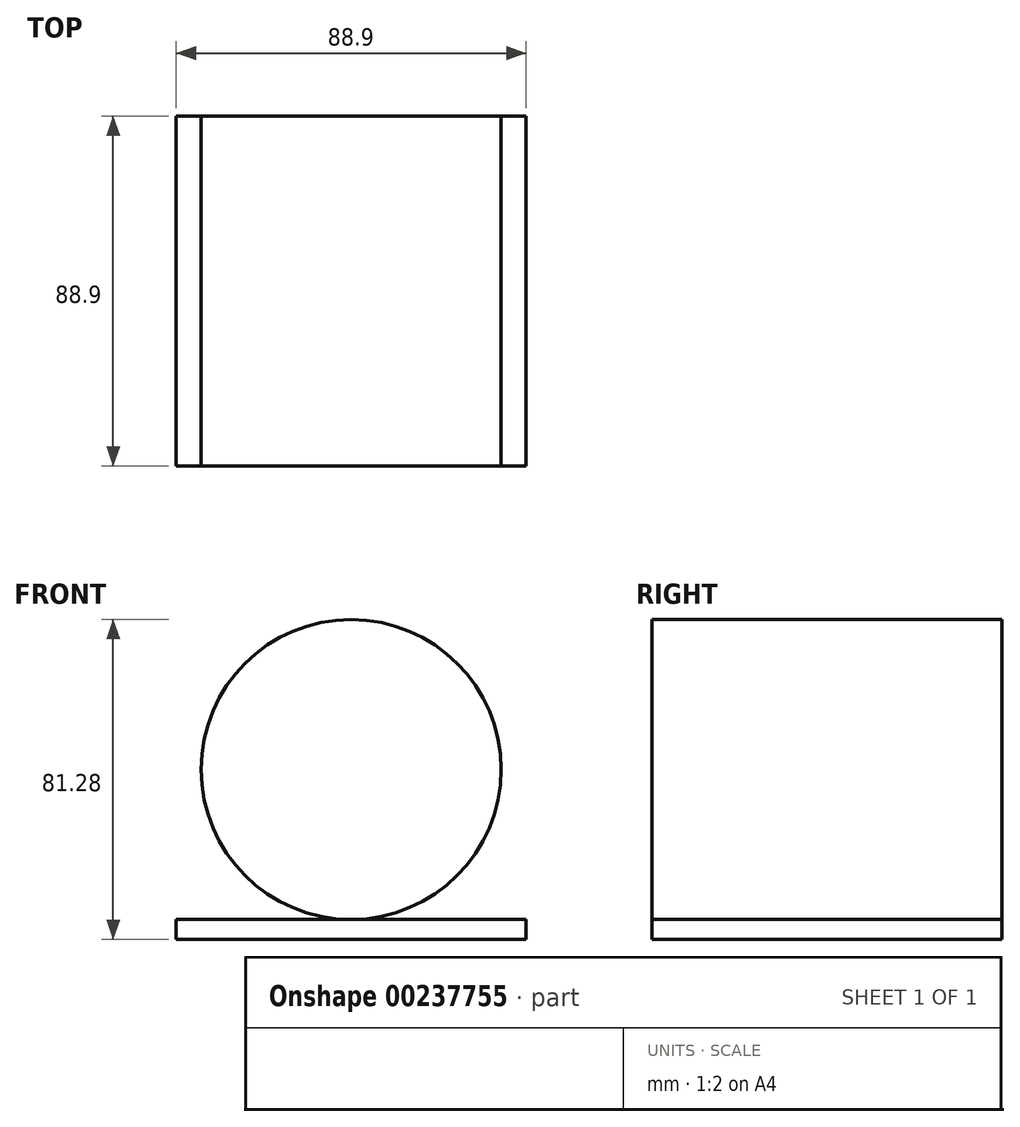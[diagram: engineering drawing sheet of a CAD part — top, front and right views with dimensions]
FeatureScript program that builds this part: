
annotation { "Feature Type Name" : "Feature", "Feature Type Description" : "" }
export const myFeature = defineFeature(function(context is Context, id is Id, definition is map)
    precondition{}
    {
        {
            var Q0;
            Q0=qCreatedBy(makeId("Front.planeOp"),FACE);
            var sketch = newSketch(context, id + "F0", { "sketchPlane" : qUnion([Q0])});
            skCircle(sketch, "E0", {"center": v(0, -7.77) * mm, "radius": 38.1 * mm});
            skLineSegment(sketch, "E1.bottom", {"start": v(-44.45, -45.87) * mm, "end": v(44.45, -45.87) * mm});
            skLineSegment(sketch, "E1.top", {"start": v(-44.45, -50.95) * mm, "end": v(44.45, -50.95) * mm});
            skLineSegment(sketch, "E1.left", {"start": v(-44.45, -45.87) * mm, "end": v(-44.45, -50.95) * mm});
            skLineSegment(sketch, "E1.right", {"start": v(44.45, -45.87) * mm, "end": v(44.45, -50.95) * mm});
            skSolve(sketch);
        }
        {
            var Q0;
            {var subQ0=sQuery(id+"F0.wireOp",EDGE,"DU6uzVH8-NPqm-Om2P-tgr6-648kfvqvj1Ei");var subQ1=makeQuery(id+"F0.imprint","INTERSECT",VERTEX,{"derivedFrom":[subQ0,sQuery(id+"F0.wireOp",EDGE,"E0")]});Q0=makeQuery(id+"F0.imprint","IMPRINT",FACE,{"disambiguationData":[TD([[makeQuery(id+"F0.imprint","IMPRINT",EDGE,{"disambiguationData":[TD([[subQ1,1.0]])],"derivedFrom":subQ0}),1.0]])]});}
            var Q1;
            {var subQ0=sQuery(id+"F0.wireOp",EDGE,"699bd6fe-4fd1-4dce-9f90-8813f1e17c5f");var subQ1=makeQuery(id+"F0.imprint","INTERSECT",VERTEX,{"derivedFrom":[sQuery(id+"F0.wireOp",EDGE,"DU6uzVH8-NPqm-Om2P-tgr6-648kfvqvj1Ei"),subQ0]});Q1=makeQuery(id+"F0.imprint","IMPRINT",FACE,{"disambiguationData":[TD([[makeQuery(id+"F0.imprint","IMPRINT",EDGE,{"disambiguationData":[TD([[subQ1,-1.0]])],"derivedFrom":subQ0}),1.0]])]});}
            var Q2;
            {var subQ0=sQuery(id+"F0.wireOp",EDGE,"9414e734-b9f1-44fd-b29a-d7e3204a8d60");var subQ4=makeQuery(id+"F0.imprint","INTERSECT",VERTEX,{"derivedFrom":[sQuery(id+"F0.wireOp",EDGE,"699bd6fe-4fd1-4dce-9f90-8813f1e17c5f"),subQ0]});Q2=makeQuery(id+"F0.imprint","IMPRINT",FACE,{"disambiguationData":[TD([[makeQuery(id+"F0.imprint","IMPRINT",EDGE,{"disambiguationData":[TD([[subQ4,1.0]])],"derivedFrom":subQ0}),1.0]])]});}
            var Q3;
            {var subQ0=sQuery(id+"F0.wireOp",EDGE,"01eb658d-8cb0-4c16-9e74-70905ed8b878");var subQ1=makeQuery(id+"F0.imprint","INTERSECT",VERTEX,{"derivedFrom":[sQuery(id+"F0.wireOp",EDGE,"699bd6fe-4fd1-4dce-9f90-8813f1e17c5f"),subQ0]});Q3=makeQuery(id+"F0.imprint","IMPRINT",FACE,{"disambiguationData":[TD([[makeQuery(id+"F0.imprint","IMPRINT",EDGE,{"disambiguationData":[TD([[subQ1,-1.0]])],"derivedFrom":subQ0}),1.0]])]});}
            var Q4;
            {var subQ0=sQuery(id+"F0.wireOp",EDGE,"E0");var subQ1=makeQuery(id+"F0.imprint","INTERSECT",VERTEX,{"derivedFrom":[sQuery(id+"F0.wireOp",EDGE,"DU6uzVH8-NPqm-Om2P-tgr6-648kfvqvj1Ei"),subQ0]});Q4=makeQuery(id+"F0.imprint","IMPRINT",FACE,{"disambiguationData":[TD([[makeQuery(id+"F0.imprint","IMPRINT",EDGE,{"disambiguationData":[TD([[subQ1,1.0]])],"derivedFrom":subQ0}),1.0]])]});}
            var Q5;
            Q5=makeQuery(id+"F0.imprint","IMPRINT",FACE,{"disambiguationData":[TD([[makeQuery(id+"F0.imprint","IMPRINT",EDGE,{"derivedFrom":sQuery(id+"F0.wireOp",EDGE,"E1.top")}),1.0]])]});
            var Q6;
            Q6=sQuery(id+"F0.wireOp",EDGE,"DU6uzVH8-NPqm-Om2P-tgr6-648kfvqvj1Ei");
            var Q7;
            Q7=sQuery(id+"F0.wireOp",EDGE,"699bd6fe-4fd1-4dce-9f90-8813f1e17c5f");
            var Q8;
            Q8=sQuery(id+"F0.wireOp",EDGE,"E0");
            var Q9;
            Q9=sQuery(id+"F0.wireOp",EDGE,"9414e734-b9f1-44fd-b29a-d7e3204a8d60");
            var Q10;
            Q10=sQuery(id+"F0.wireOp",EDGE,"01eb658d-8cb0-4c16-9e74-70905ed8b878");
            var Q11;
            Q11=sQuery(id+"F0.wireOp",EDGE,"E1.bottom");
            var Q12;
            Q12=sQuery(id+"F0.wireOp",EDGE,"E1.top");
            var Q13;
            Q13=sQuery(id+"F0.wireOp",EDGE,"E1.left");
            var Q14;
            Q14=sQuery(id+"F0.wireOp",EDGE,"E1.right");
            extrude(context, id + "F1", {"entities" : qUnion([Q0, Q1, Q2, Q3, Q4, Q5]), "surfaceEntities" : qUnion([Q6, Q7, Q8, Q9, Q10, Q11, Q12, Q13, Q14]), "depth" : 88.9 * mm});
        }
    });
